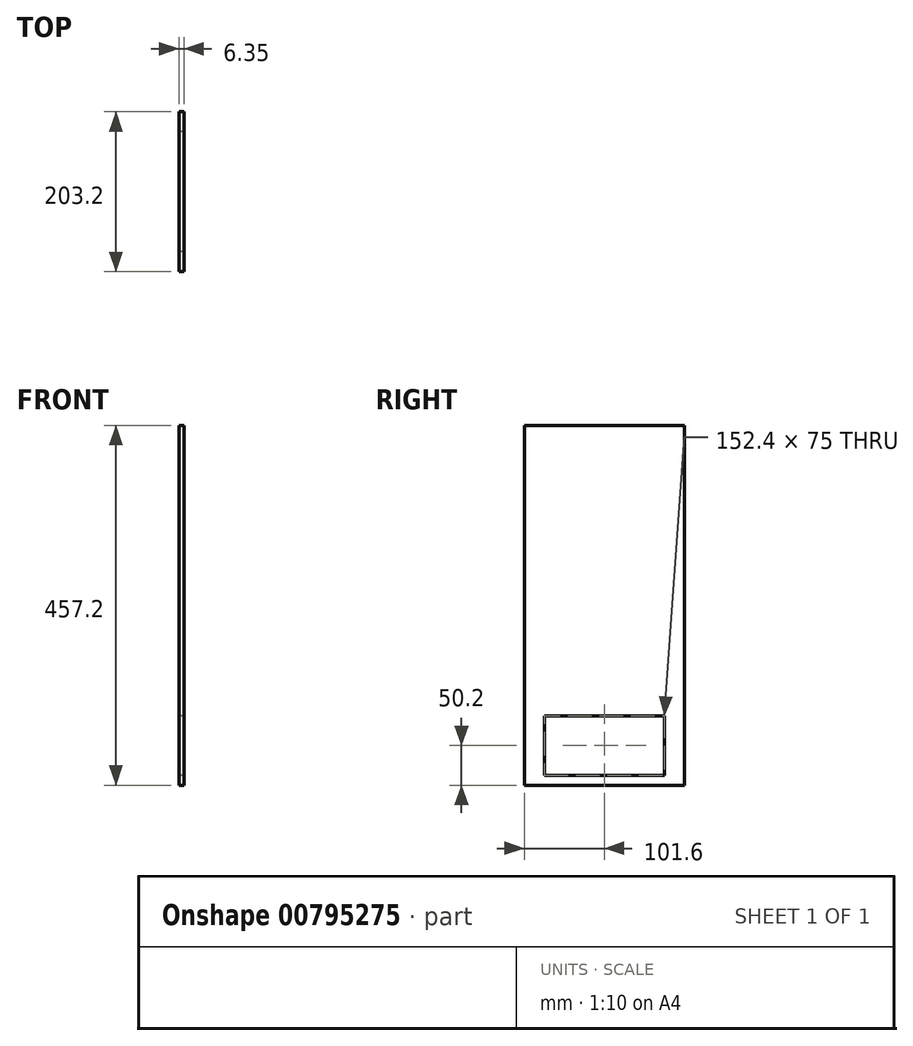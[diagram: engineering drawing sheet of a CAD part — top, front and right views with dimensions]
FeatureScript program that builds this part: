
annotation { "Feature Type Name" : "Feature", "Feature Type Description" : "" }
export const myFeature = defineFeature(function(context is Context, id is Id, definition is map)
    precondition{}
    {
        {
            var Q0;
            Q0=qCreatedBy(makeId("Right.planeOp"),FACE);
            var sketch = newSketch(context, id + "F0", { "sketchPlane" : qUnion([Q0])});
            skLineSegment(sketch, "E0.bottom", {"start": v(101.6, -228.6) * mm, "end": v(-101.6, -228.6) * mm});
            skLineSegment(sketch, "E0.top", {"start": v(101.6, 228.6) * mm, "end": v(-101.6, 228.6) * mm});
            skLineSegment(sketch, "E0.left", {"start": v(101.6, -228.6) * mm, "end": v(101.6, 228.6) * mm});
            skLineSegment(sketch, "E0.right", {"start": v(-101.6, -228.6) * mm, "end": v(-101.6, 228.6) * mm});
            skPoint(sketch, "E0.middle", {"position": v(0, 0) * mm});
            skLineSegment(sketch, "E1.bottom", {"start": v(-76.2, -140.9) * mm, "end": v(76.2, -140.9) * mm});
            skLineSegment(sketch, "E1.top", {"start": v(-76.2, -215.9) * mm, "end": v(76.2, -215.9) * mm});
            skLineSegment(sketch, "E1.left", {"start": v(-76.2, -140.9) * mm, "end": v(-76.2, -215.9) * mm});
            skLineSegment(sketch, "E1.right", {"start": v(76.2, -140.9) * mm, "end": v(76.2, -215.9) * mm});
            skLineSegment(sketch, "E2", {"start": v(-101.6, -173.27) * mm, "end": v(-76.2, -173.27) * mm, "construction": true});
            skPoint(sketch, "E2.endSnap0", {"position": v(-76.2, -178.4) * mm});
            skLineSegment(sketch, "E3", {"start": v(76.2, -178.4) * mm, "end": v(101.6, -178.4) * mm, "construction": true});
            skSolve(sketch);
        }
        {
            var Q0;
            Q0=makeQuery(id+"F0.imprint","IMPRINT",FACE,{"disambiguationData":[TD([[makeQuery(id+"F0.imprint","IMPRINT",EDGE,{"derivedFrom":sQuery(id+"F0.wireOp",EDGE,"E0.top")}),1.0]])]});
            extrude(context, id + "F1", {"entities" : qUnion([Q0]), "depth" : 6.35 * mm, "offsetDistance" : 25.4 * mm});
        }
    });
